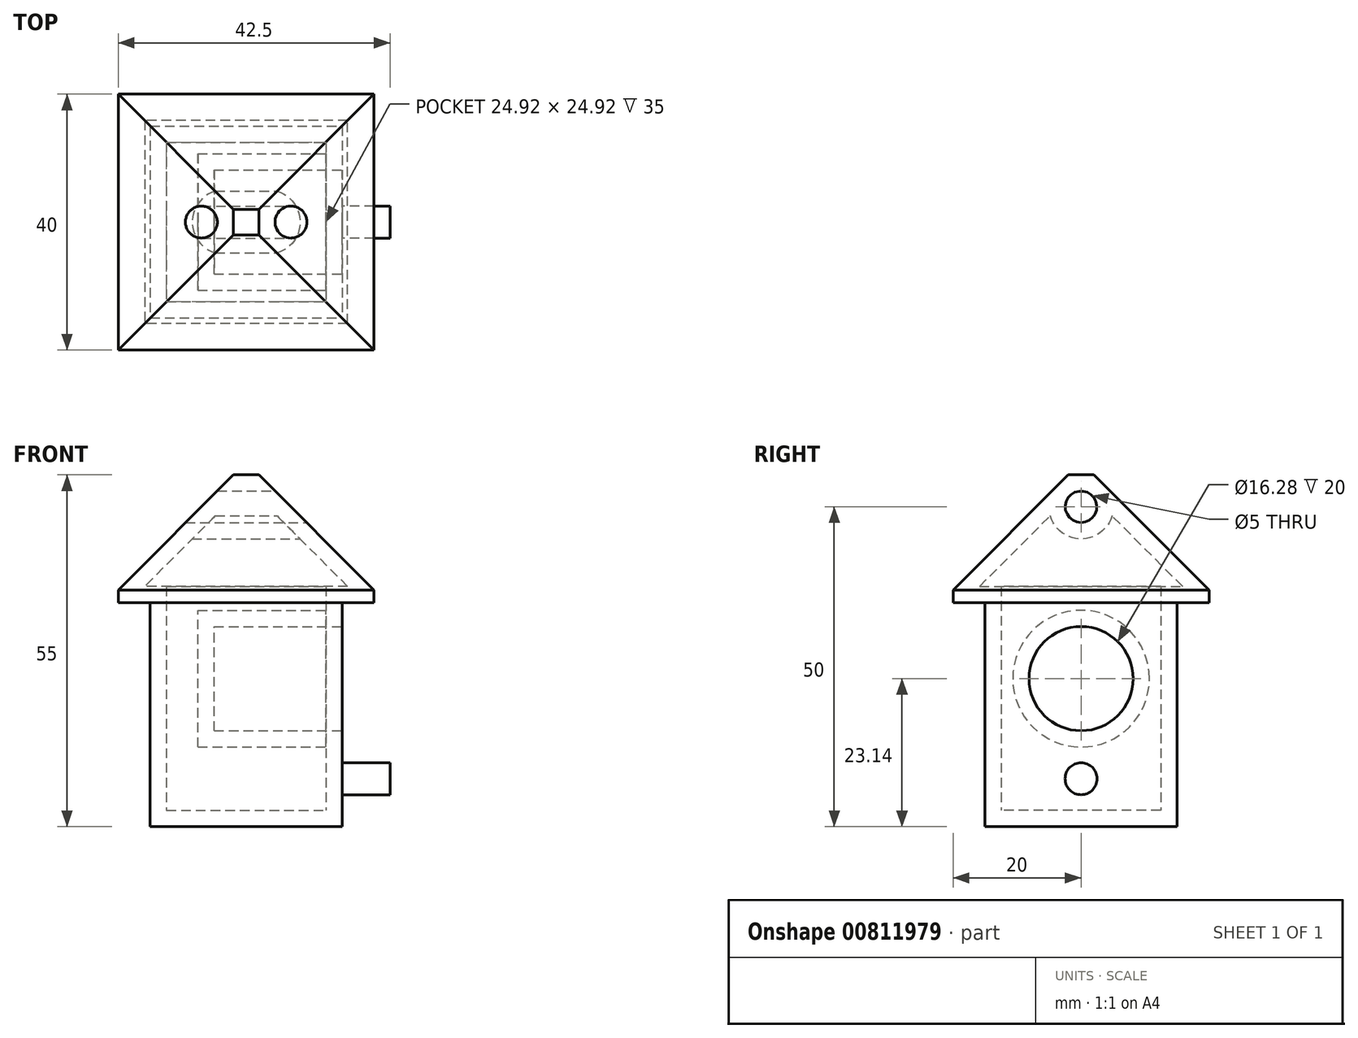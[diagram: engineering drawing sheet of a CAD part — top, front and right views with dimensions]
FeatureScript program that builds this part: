
annotation { "Feature Type Name" : "Feature", "Feature Type Description" : "" }
export const myFeature = defineFeature(function(context is Context, id is Id, definition is map)
    precondition{}
    {
        {
            var Q0;
            Q0=qCreatedBy(makeId("Top.planeOp"),FACE);
            var sketch = newSketch(context, id + "F0", { "sketchPlane" : qUnion([Q0])});
            skLineSegment(sketch, "E0.bottom", {"start": v(-15, 15) * mm, "end": v(15, 15) * mm});
            skLineSegment(sketch, "E0.top", {"start": v(-15, -15) * mm, "end": v(15, -15) * mm});
            skLineSegment(sketch, "E0.left", {"start": v(-15, 15) * mm, "end": v(-15, -15) * mm});
            skLineSegment(sketch, "E0.right", {"start": v(15, 15) * mm, "end": v(15, -15) * mm});
            skPoint(sketch, "E0.middle", {"position": v(0, 0) * mm});
            skSolve(sketch);
        }
        {
            var Q0;
            Q0=qSketchRegion(id+"F0",true);
            extrude(context, id + "F1", {"entities" : qUnion([Q0]), "depth" : 35 * mm, "offsetDistance" : 25.4 * mm});
        }
        {
            var Q0;
            Q0=makeQuery(id+"F1.opExtrude","CAP_FACE",FACE,{"disambiguationData":[OSD([sQuery(id+"F0.wireOp",EDGE,"E0.bottom"),sQuery(id+"F0.wireOp",EDGE,"E0.top"),sQuery(id+"F0.wireOp",EDGE,"E0.left"),sQuery(id+"F0.wireOp",EDGE,"E0.right")])],"isStart":false});
            var sketch = newSketch(context, id + "F2", { "sketchPlane" : qUnion([Q0])});
            skLineSegment(sketch, "E1.bottom", {"start": v(20, 20) * mm, "end": v(-20, 20) * mm});
            skLineSegment(sketch, "E1.top", {"start": v(20, -20) * mm, "end": v(-20, -20) * mm});
            skLineSegment(sketch, "E1.left", {"start": v(20, 20) * mm, "end": v(20, -20) * mm});
            skLineSegment(sketch, "E1.right", {"start": v(-20, 20) * mm, "end": v(-20, -20) * mm});
            skPoint(sketch, "E1.middle", {"position": v(0, 0) * mm});
            skSolve(sketch);
        }
        {
            var Q0;
            Q0=qSketchRegion(id+"F2",true);
            extrude(context, id + "F3", {"entities" : qUnion([Q0]), "operationType" : NewBodyOperationType.ADD, "depth" : 20 * mm, "offsetDistance" : 25.4 * mm});
        }
        {
            var Q0;
            Q0=makeQuery(id+"F3.opExtrude","CAP_EDGE",EDGE,{"disambiguationData":[OSD([sQuery(id+"F2.wireOp",EDGE,"E1.left")])],"isStart":false});
            var Q1;
            Q1=makeQuery(id+"F3.opExtrude","CAP_EDGE",EDGE,{"disambiguationData":[OSD([sQuery(id+"F2.wireOp",EDGE,"E1.bottom")])],"isStart":false});
            var Q2;
            Q2=makeQuery(id+"F3.opExtrude","CAP_EDGE",EDGE,{"disambiguationData":[OSD([sQuery(id+"F2.wireOp",EDGE,"E1.right")])],"isStart":false});
            var Q3;
            Q3=makeQuery(id+"F3.opExtrude","CAP_FACE",FACE,{"disambiguationData":[OSD([sQuery(id+"F2.wireOp",EDGE,"E1.bottom"),sQuery(id+"F2.wireOp",EDGE,"E1.top"),sQuery(id+"F2.wireOp",EDGE,"E1.left"),sQuery(id+"F2.wireOp",EDGE,"E1.right")])],"isStart":false});
            chamfer(context, id + "F4", {"entities" : qUnion([Q0, Q1, Q2, Q3]), "width" : 18 * mm, "tangentPropagation" : true});
        }
        {
            var Q0;
            Q0=makeQuery(id+"F1.opExtrude","SWEPT_FACE",FACE,{"disambiguationData":[OSD([sQuery(id+"F0.wireOp",EDGE,"E0.right")])]});
            var sketch = newSketch(context, id + "F5", { "sketchPlane" : qUnion([Q0])});
            skCircle(sketch, "E2", {"center": v(0, 23.14) * mm, "radius": 8.14 * mm});
            skPoint(sketch, "E2.first.point", {"position": v(-5.35, 17) * mm});
            skPoint(sketch, "E2.second.point", {"position": v(5, 16.72) * mm});
            skPoint(sketch, "E2.third.point", {"position": v(0, 31.28) * mm});
            skSolve(sketch);
        }
        {
            var Q0;
            Q0=qSketchRegion(id+"F5",true);
            var Q1;
            Q1=sQuery(id+"F5.wireOp",EDGE,"E2");
            extrude(context, id + "F6", {"entities" : qUnion([Q0]), "operationType" : NewBodyOperationType.REMOVE, "surfaceOperationType" : NewSurfaceOperationType.ADD, "surfaceEntities" : qUnion([Q1]), "oppositeDirection" : true, "depth" : 20 * mm, "offsetDistance" : 25.4 * mm});
        }
        {
            var Q0;
            Q0=makeQuery(id+"F1.opExtrude","SWEPT_FACE",FACE,{"disambiguationData":[OSD([sQuery(id+"F0.wireOp",EDGE,"E0.right")])]});
            var sketch = newSketch(context, id + "F7", { "sketchPlane" : qUnion([Q0])});
            skCircle(sketch, "E3", {"center": v(0, 7.5) * mm, "radius": 2.5 * mm});
            skSolve(sketch);
        }
        {
            var Q0;
            Q0=makeQuery(id+"F7.imprint","IMPRINT",FACE,{"disambiguationData":[TD([[makeQuery(id+"F7.imprint","IMPRINT",EDGE,{"derivedFrom":sQuery(id+"F7.wireOp",EDGE,"E3")}),1.0]])]});
            var Q1;
            Q1=qSketchRegion(id+"F9",true);
            extrude(context, id + "F8", {"entities" : qUnion([Q0, Q1]), "operationType" : NewBodyOperationType.ADD, "depth" : 7.5 * mm, "offsetDistance" : 25.4 * mm});
        }
        {
            var Q0;
            Q0=makeQuery(id+"F3.opExtrude","SWEPT_FACE",FACE,{"disambiguationData":[OSD([sQuery(id+"F2.wireOp",EDGE,"E1.left")])]});
            var sketch = newSketch(context, id + "F9", { "sketchPlane" : qUnion([Q0])});
            skCircle(sketch, "E4", {"center": v(0, 50) * mm, "radius": 2.5 * mm});
            skSolve(sketch);
        }
        {
            var Q0;
            Q0=makeQuery(id+"F9.imprint","IMPRINT",FACE,{"disambiguationData":[TD([[makeQuery(id+"F9.imprint","IMPRINT",EDGE,{"derivedFrom":sQuery(id+"F9.wireOp",EDGE,"E4")}),1.0]])]});
            extrude(context, id + "F10", {"entities" : qUnion([Q0]), "operationType" : NewBodyOperationType.REMOVE, "oppositeDirection" : true, "depth" : 79.5 * mm, "offsetDistance" : 25.4 * mm});
        }
        {
            var Q0;
            Q0=makeQuery(id+"F4.opChamfer","BLEND_FACE",FACE,{"disambiguationData":[OSD([sQuery(id+"F2.wireOp",EDGE,"E1.top")])]});
            var Q1;
            Q1=makeQuery(id+"F1.opExtrude","SWEPT_BODY",BODY,{"disambiguationData":[OSD([sQuery(id+"F0.wireOp",EDGE,"E0.bottom"),sQuery(id+"F0.wireOp",EDGE,"E0.top"),sQuery(id+"F0.wireOp",EDGE,"E0.left"),sQuery(id+"F0.wireOp",EDGE,"E0.right")])]});
            shell(context, id + "F11", {"isHollow" : true, "entities" : qUnion([Q0]), "parts" : qUnion([Q1]), "thickness" : 2.54 * mm});
        }
    });
